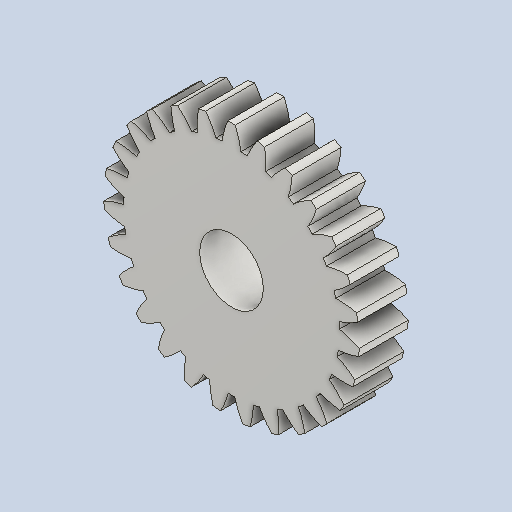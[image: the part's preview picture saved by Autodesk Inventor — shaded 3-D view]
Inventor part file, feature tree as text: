
AUTODESK INVENTOR PART (.ipt)
format: ipt  version: 2022 (Build 260153000, 153)  size: 284,672 bytes
history: native  units: mm (DEFAULTED — no unit token found)
features: plane x3, other x3, sketch x2, extrude x1
ambient origin geometry x8: Origin, YZ Plane, XZ Plane, XY Plane, X Axis, Y Axis, Z Axis, Center Point
bodies: Solid1 (feature_tree)
feature tree (9):
  extrude  "Extrusion1"  Depth=5.0mm TaperAngle=0.0deg
  plane  "Work Plane2"
  plane  "Work Plane8"
  plane  "Work Plane9"
  other  "Spur Gear"
  sketch  "Sketch1"  dims[d0=26.081577mm d1=5.0mm d2=0.0mm]
  sketch  "Sketch2"  dims[d3=24.3mm d4=10.0mm d5=0.0mm d16=25.0mm d17=0.0mm d34=1.163553mm d39=0.0mm d41=0.0mm d43=25.0mm d46=25.0mm d47=0.0mm d48=0.0mm d49=6.5mm]
  other  "Srf1"
  other  "Pitch Diameter"
